# Revit family: ARENA POINTS
name_source: partatom
category: Generic Models
units: mm (PartAtom-declared; Revit-internal decimal feet)

## family parameters
Always vertical = Yes
Can host rebar = No
Cut with Voids When Loaded = No
Part Type = Normal
Room Calculation Point = No
Round Connector Dimension = Use Diameter
Shared = No
Work Plane-Based = No

## types (14) — shared parameters
ARENA POINT GAP = 130 mm
Arena QTY per panel = 6
Arena points total = 12
C2C = 2400 mm
End gap = 50 mm  [stored 0.164042 ft]
Fixing Height = 247 mm
Glass Height = 1200 mm  [stored 3.93701 ft]
Glass Thickness = 15 mm  [stored 0.0492126 ft]
Hand rail QTY = 2
Hand rail space = 1000 mm  [stored 3.28084 ft]
Length = 2500 mm
Max Panel Size = 1400 mm
Panel QTY = 2
Panel Size = 1200 mm  [stored 3.93701 ft]
Spacer Depth = 50 mm  [stored 0.164042 ft]
hand rail height = 850 mm  [stored 2.78871 ft]
zero-valued in all types: Default Elevation

## per-type parameters (varying)
| type | ARN (Top rail) | ART (Top rail) | ART (side fix) | Description | Hand rail brackets | Keynote | LRR ( Side fix Round hand rail) | LRS (Top rail) | Manufacturer | Model | PRR (Top Rail) | PRR(Side fix) | URL | VRE (Side fix) | VRE (Top rail) | VRR (Side fix) | VRR (Top rail) | VRT (Top rail) | VRT(Side fix) |
| Arena ( No Rails)*Sentry glass only | No | No | No | UNEX ARENA POINTS FRAMELESS GLASS WITH NO TOP RAIL | No | UNEX SYSTEMS, ARENA POINTS SIDE FIX BALUSTRADE | No | No | UNEX SYSTEMS | UNEX, ARENA POINTS SIDE FIX | No | No | WWW.UNEX.CO.NZ | No | No | No | No | No | No |
| Arena (ARN Top rail) | Yes | No | No | UNEX ARENA POINTS FRAMELESS GLASS WITH ARN TOP RAIL | No | UNEX SYSTEMS, ARENA POINTS SIDE FIX BALUSTRADE | No | No | UNEX SYSTEMS | UNEX, ARENA POINTS SIDE FIX (ARN) | No | No | WWW.UNEX.CO.NZ | No | No | No | No | No | No |
| Arena (ART Top rail) | No | Yes | No |  | No |  | No | No |  |  | No | No |  | No | No | No | No | No | No |
| Arena (PRR Top rail) | No | No | No | UNEX ARENA POINTS FRAMELESS GLASS WITH PRR TOP RAIL | No | UNEX SYSTEMS, ARENA POINTS SIDE FIX BALUSTRADE | No | No | UNEX SYSTEMS | UNEX, ARENA POINTS SIDE FIX (PRR) | Yes | No | WWW.UNEX.CO.NZ | No | No | No | No | No | No |
| Arena (VRE Top rail) | No | No | No | UNEX ARENA POINTS FRAMELESS GLASS WITH VRE TOP RAIL | No | UNEX SYSTEMS, ARENA POINTS SIDE FIX BALUSTRADE | No | No | UNEX SYSTEMS | UNEX, ARENA POINTS SIDE FIX (VRE) | No | No | WWW.UNEX.CO.NZ | No | Yes | No | No | No | No |
| Arena (VRR Top rail) | No | No | No | UNEX ARENA POINTS FRAMELESS GLASS WITH VRR TOP RAIL | No | UNEX SYSTEMS, ARENA POINTS SIDE FIX BALUSTRADE | No | No | UNEX SYSTEMS | UNEX, ARENA POINTS SIDE FIX (VRR) | No | No | WWW.UNEX.CO.NZ | No | No | No | Yes | No | No |
| Arena (VRT Top rail) | No | No | No | UNEX ARENA POINTS FRAMELESS GLASS WITH VRT TOP RAIL | No | UNEX SYSTEMS, ARENA POINTS SIDE FIX BALUSTRADE | No | No | UNEX SYSTEMS | UNEX, ARENA POINTS SIDE FIX (VRT) | No | No | WWW.UNEX.CO.NZ | No | No | No | No | Yes | No |
| Arena ( LRR side rail) *Sentry glass only | No | No | No | UNEX ARENA POINTS FRAMELESS GLASS WITH LRR SIDE RAIL | Yes | UNEX SYSTEMS, ARENA POINTS SIDE FIX BALUSTRADE | Yes | No | UNEX SYSTEMS | UNEX, ARENA POINTS SIDE FIX (LRR) | No | No | WWW.UNEX.CO.NZ | No | No | No | No | No | No |
| Arena (LRS Top rail) | No | No | No | UNEX ARENA POINTS FRAMELESS GLASS WITH LRS TOP RAIL | No | UNEX SYSTEMS, ARENA POINTS SIDE FIX BALUSTRADE | No | Yes | UNEX SYSTEMS | UNEX, ARENA POINTS SIDE FIX  (LRS) | No | No | WWW.UNEX.CO.NZ | No | No | No | No | No | No |
| Arena (ART Side fix) | No | No | Yes | UNEX ARENA POINTS FRAMELESS GLASS WITH ART SIDE RAIL | Yes | UNEX SYSTEMS, ARENA POINTS SIDE FIX BALUSTRADE | No | No | UNEX SYSTEMS | UNEX, ARENA POINTS SIDE FIX & SIDE (ART) | No | No | WWW.UNEX.CO.NZ | No | No | No | No | No | No |
| Arena (PRR Side fix) | No | No | No | UNEX ARENA POINTS FRAMELESS GLASS WITH PRR SIDE RAIL | Yes | UNEX SYSTEMS, ARENA POINTS SIDE FIX BALUSTRADE | No | No | UNEX SYSTEMS | UNEX, ARENA POINTS SIDE FIX & SIDE (PRR) | No | Yes | WWW.UNEX.CO.NZ | No | No | No | No | No | No |
| Arena ( VRE side rail )*Sentry glass only | No | No | No | UNEX ARENA POINTS FRAMELESS GLASS WITH VRE SIDE RAIL | Yes | UNEX SYSTEMS, ARENA POINTS SIDE FIX BALUSTRADE | No | No | UNEX SYSTEMS | UNEX, ARENA POINTS SIDE FIX  & SIDE (VRE) | No | No | WWW.UNEX.CO.NZ | Yes | No | No | No | No | No |
| Arena ( VRR side rail )*Sentry glass only | No | No | No | UNEX ARENA POINTS FRAMELESS GLASS WITH VRR SIDE RAIL | Yes | UNEX SYSTEMS, ARENA POINTS SIDE FIX BALUSTRADE | No | No | UNEX SYSTEMS | UNEX, ARENA POINTS SIDE FIX & SIDE  (VRR) | No | No | WWW.UNEX.CO.NZ | No | No | Yes | No | No | No |
| Arena ( VRT side rail )*Sentry glass only | No | No | No | UNEX ARENA POINTS FRAMELESS GLASS WITH VRT SIDE RAIL | Yes | UNEX SYSTEMS, ARENA POINTS SIDE FIX BALUSTRADE | No | No | UNEX SYSTEMS | UNEX, ARENA POINTS SIDE FIX & SIDE (VRT) | No | No | WWW.UNEX.CO.NZ | No | No | No | No | No | Yes |

note: [stored X ft] marks values corroborated as IEEE doubles in the binary element streams (Revit-internal decimal feet)

## geometry (parser evidence)
native form markers: Sweep x36
no freeform markers — native parametric forms only
